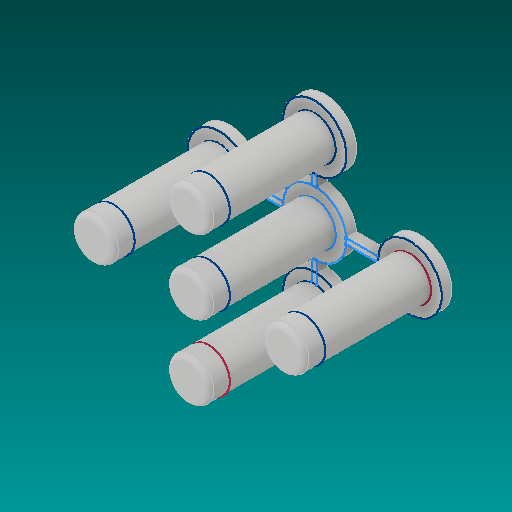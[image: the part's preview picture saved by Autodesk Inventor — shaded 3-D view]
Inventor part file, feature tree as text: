
AUTODESK INVENTOR PART (.ipt)
format: ipt  version: 2019 (Build 230136000, 136)  size: 246,784 bytes
history: native  units: mm
features: other x6, sketch x4
ambient origin geometry x8: Origin, YZ Plane, XZ Plane, XY Plane, X Axis, Y Axis, Z Axis, Center Point
bodies: Solid1 (feature_tree), Solid2 (feature_tree), Solid3 (feature_tree), Solid4 (feature_tree), Solid5 (feature_tree), Solid6 (feature_tree), Solid144 (feature_tree)
feature tree (10):
  other  "Repaired Geometry1"
  sketch  "Sketch13"
  sketch  "Sketch9"
  sketch  "Sketch10"
  sketch  "Sketch8"
  other  "Solid144:1"
  other  "Solid144:2"
  other  "Solid144:3"
  other  "Solid144:4"
  other  "Solid144:5"
